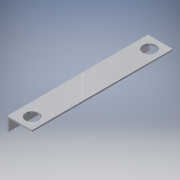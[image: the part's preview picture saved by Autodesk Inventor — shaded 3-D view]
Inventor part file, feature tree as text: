
AUTODESK INVENTOR PART (.ipt)
format: ipt  version: 2016 (Build 200138000, 138)  size: 114,688 bytes
history: native  units: in
note: dims shown in document units (in); Inventor stores cm internally (conversion verified against a paired STEP export)
features: extrude x3, sketch x3
ambient origin geometry x8: Origin, YZ Plane, XZ Plane, XY Plane, X Axis, Y Axis, Z Axis, Center Point
bodies: Solid1 (feature_tree)
feature tree (6):
  extrude  "Extrusion1"  Depth=2.0in
  extrude  "Extrusion2"  Depth=1.0in
  extrude  "Extrusion3"  Depth=1.0in
  sketch  "Sketch1"  dims[d0=12.0in d1=2.0in]
  sketch  "Sketch2"  dims[d2=1.0in d3=1.0in]
  sketch  "Sketch3"  dims[d4=1.0in d5=1.0in d6=1.125in d7=1.125in d8=0.125in d9=0.0in d10=0.125in d11=0.0in d12=1.0in d13=0.0in]
